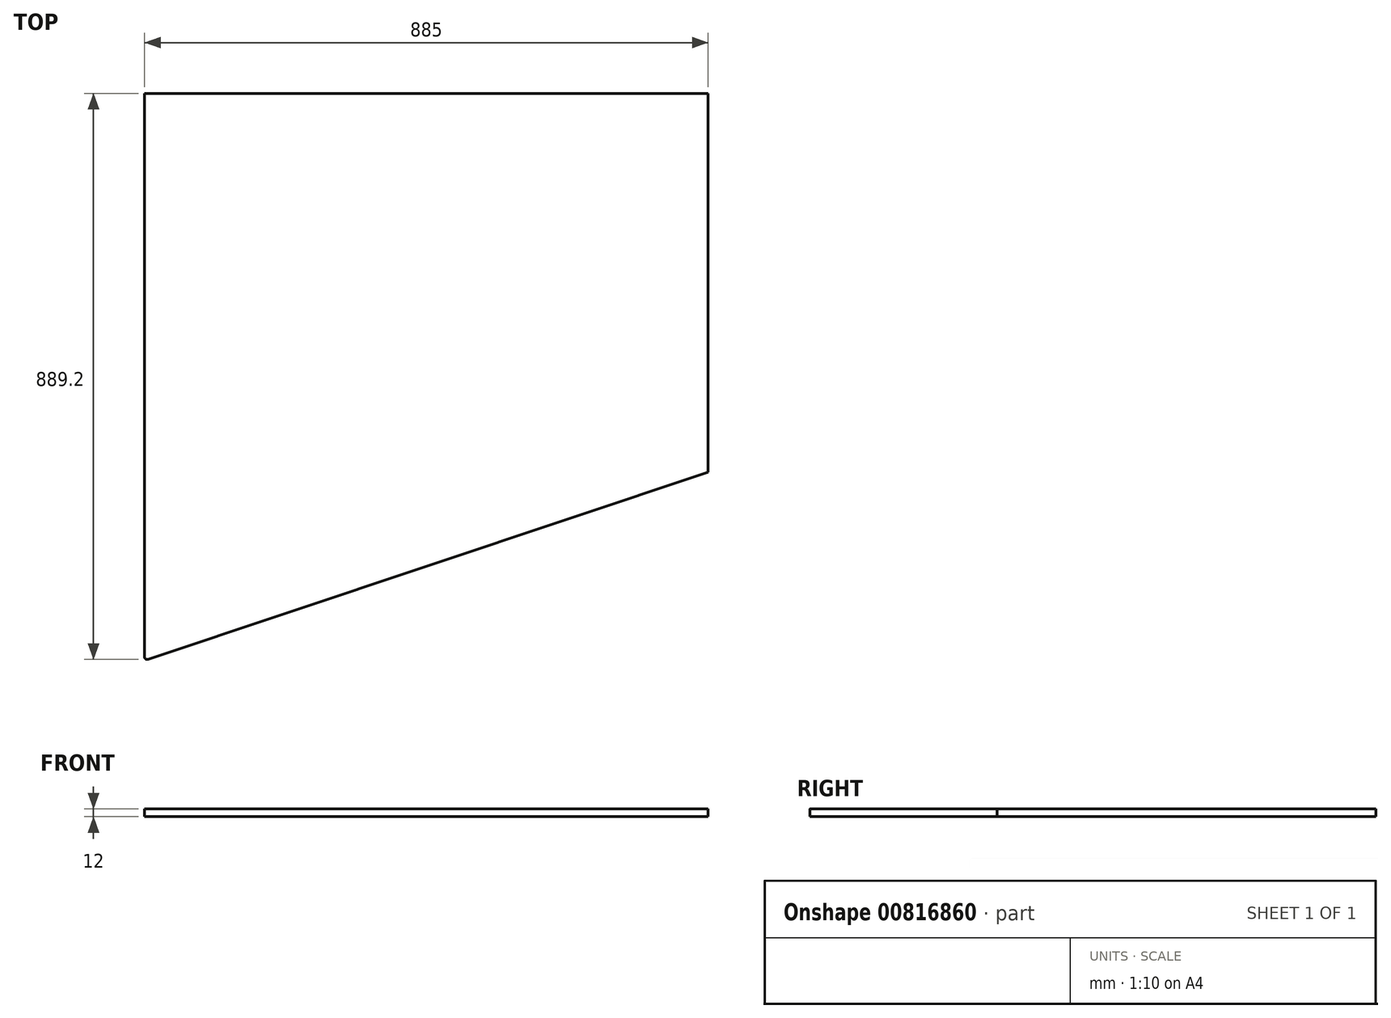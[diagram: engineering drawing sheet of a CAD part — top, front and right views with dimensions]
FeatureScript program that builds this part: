
annotation { "Feature Type Name" : "Feature", "Feature Type Description" : "" }
export const myFeature = defineFeature(function(context is Context, id is Id, definition is map)
    precondition{}
    {
        {
            var Q0;
            Q0=qCreatedBy(makeId("Top.planeOp"),FACE);
            var sketch = newSketch(context, id + "F0", { "sketchPlane" : qUnion([Q0])});
            skLineSegment(sketch, "E0", {"start": v(0, 0) * mm, "end": v(0, -890.76) * mm});
            skLineSegment(sketch, "E1", {"start": v(0, -890.76) * mm, "end": v(885, -595) * mm});
            skLineSegment(sketch, "E2", {"start": v(885, -595) * mm, "end": v(885, 0) * mm});
            skLineSegment(sketch, "E3", {"start": v(885, 0) * mm, "end": v(0, 0) * mm});
            skPoint(sketch, "E4", {"position": v(107, -855) * mm});
            skSolve(sketch);
        }
        {
            var Q0;
            Q0=makeQuery(id+"F0.imprint","IMPRINT",FACE,{"disambiguationData":[TD([[makeQuery(id+"F0.imprint","IMPRINT",EDGE,{"derivedFrom":sQuery(id+"F0.wireOp",EDGE,"E0")}),1.0]])]});
            extrude(context, id + "F1", {"entities" : qUnion([Q0]), "depth" : 12 * mm, "offsetDistance" : 25 * mm});
        }
        {
            var Q0;
            Q0=makeQuery(id+"F1.opExtrude","SWEPT_EDGE",EDGE,{"disambiguationData":[OSD([sQuery(id+"F0.wireOp",EDGE,"E0"),sQuery(id+"F0.wireOp",EDGE,"E1")])]});
            fillet(context, id + "F2", {"entities" : qUnion([Q0]), "radius" : 4 * mm, "tangentPropagation" : true, "allowEdgeOverflow" : false});
        }
    });
